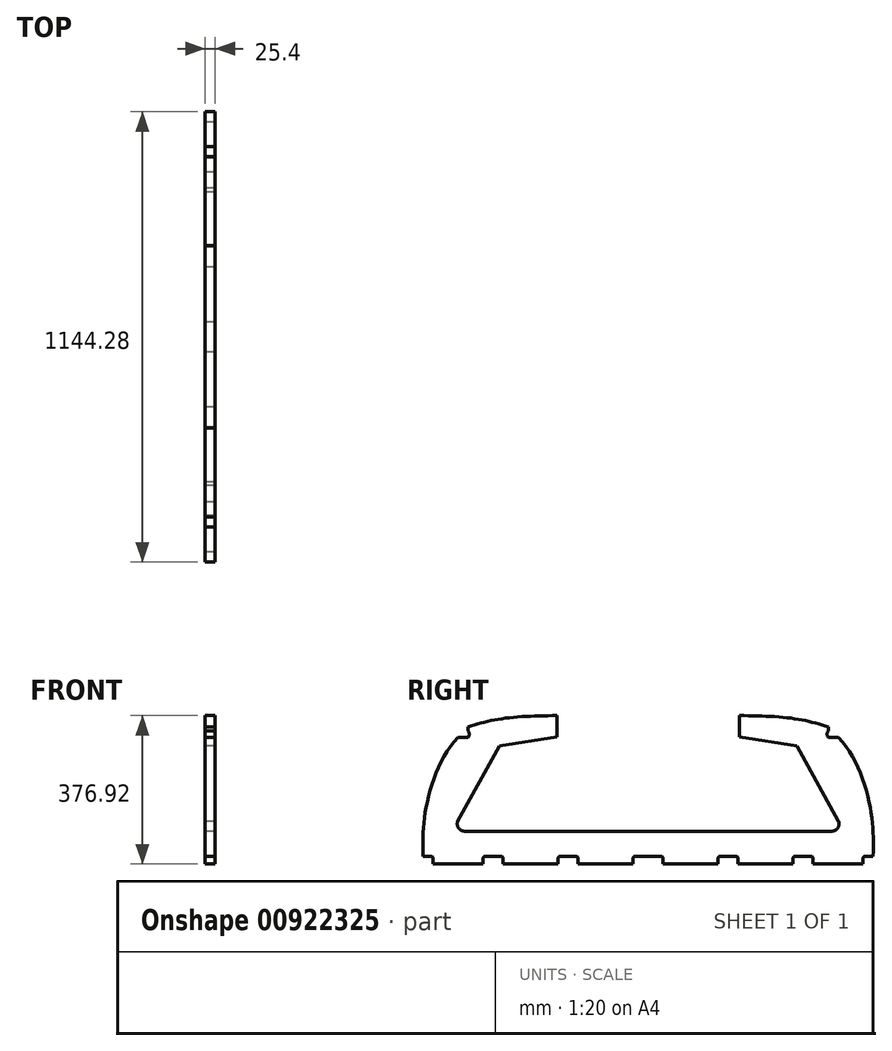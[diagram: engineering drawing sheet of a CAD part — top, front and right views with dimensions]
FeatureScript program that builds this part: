
annotation { "Feature Type Name" : "Feature", "Feature Type Description" : "" }
export const myFeature = defineFeature(function(context is Context, id is Id, definition is map)
    precondition{}
    {
        {
            var Q0;
            Q0=qCreatedBy(makeId("Right.planeOp"),FACE);
            var sketch = newSketch(context, id + "F0", { "sketchPlane" : qUnion([Q0])});
            skLineSegment(sketch, "E0", {"start": v(0, -94.79) * mm, "end": v(-33.02, -94.79) * mm});
            skLineSegment(sketch, "E1", {"start": v(-38.1, -99.87) * mm, "end": v(-38.1, -113.84) * mm});
            skLineSegment(sketch, "E2", {"start": v(-38.1, -113.84) * mm, "end": v(-177.8, -113.84) * mm});
            skLineSegment(sketch, "E3", {"start": v(-177.8, -113.84) * mm, "end": v(-177.8, -99.87) * mm});
            skLineSegment(sketch, "E4", {"start": v(-182.88, -94.79) * mm, "end": v(-223.52, -94.79) * mm});
            skLineSegment(sketch, "E5", {"start": v(-228.6, -99.87) * mm, "end": v(-228.6, -113.84) * mm});
            skLineSegment(sketch, "E6", {"start": v(-228.6, -113.84) * mm, "end": v(-368.3, -113.84) * mm});
            skLineSegment(sketch, "E7", {"start": v(-368.3, -113.84) * mm, "end": v(-368.3, -99.87) * mm});
            skLineSegment(sketch, "E8", {"start": v(-373.38, -94.79) * mm, "end": v(-414.02, -94.79) * mm});
            skLineSegment(sketch, "E9", {"start": v(-419.1, -99.87) * mm, "end": v(-419.1, -113.84) * mm});
            skLineSegment(sketch, "E10", {"start": v(-419.1, -113.84) * mm, "end": v(-546.1, -113.84) * mm});
            skLineSegment(sketch, "E11", {"start": v(-546.1, -113.84) * mm, "end": v(-546.1, -99.87) * mm});
            skLineSegment(sketch, "E12", {"start": v(-551.18, -94.79) * mm, "end": v(-571.5, -94.79) * mm});
            skLineSegment(sketch, "E13", {"start": v(-465.99, -30.95) * mm, "end": v(0, -30.95) * mm});
            skPoint(sketch, "E14.visualSharp", {"position": v(-419.1, -94.79) * mm});
            skArc(sketch, "E14.filletArc", {"start": v(-414.02, -94.79) * mm, "mid": v(-417.61, -96.28) * mm, "end": v(-419.1, -99.87) * mm});
            skPoint(sketch, "E15.visualSharp", {"position": v(-368.3, -94.79) * mm});
            skArc(sketch, "E15.filletArc", {"start": v(-368.3, -99.87) * mm, "mid": v(-369.79, -96.28) * mm, "end": v(-373.38, -94.79) * mm});
            skPoint(sketch, "E16.visualSharp", {"position": v(-228.6, -94.79) * mm});
            skArc(sketch, "E16.filletArc", {"start": v(-223.52, -94.79) * mm, "mid": v(-227.11, -96.28) * mm, "end": v(-228.6, -99.87) * mm});
            skPoint(sketch, "E17.visualSharp", {"position": v(-177.8, -94.79) * mm});
            skArc(sketch, "E17.filletArc", {"start": v(-177.8, -99.87) * mm, "mid": v(-179.29, -96.28) * mm, "end": v(-182.88, -94.79) * mm});
            skPoint(sketch, "E18.visualSharp", {"position": v(-38.1, -94.79) * mm});
            skArc(sketch, "E18.filletArc", {"start": v(-33.02, -94.79) * mm, "mid": v(-36.61, -96.28) * mm, "end": v(-38.1, -99.87) * mm});
            skPoint(sketch, "E19.visualSharp", {"position": v(-546.1, -94.79) * mm});
            skArc(sketch, "E19.filletArc", {"start": v(-546.1, -99.87) * mm, "mid": v(-547.59, -96.28) * mm, "end": v(-551.18, -94.79) * mm});
            skPoint(sketch, "E20.visualSharp", {"position": v(-423.74, 200.49) * mm});
            skPoint(sketch, "E21.visualSharp", {"position": v(-493.39, -30.95) * mm});
            skArc(sketch, "E21.filletArc", {"start": v(-483.93, -5.23) * mm, "mid": v(-481.66, -22.77) * mm, "end": v(-465.99, -30.95) * mm});
            skArc(sketch, "E22", {"start": v(-457.61, 207.28) * mm, "mid": v(-454.45, 215.67) * mm, "end": v(-457.61, 224.06) * mm});
            skFitSpline(sketch, "E23", {"points": [v(-460.76, 233.62) * mm, v(-370.5, 255.33) * mm, v(-232.08, 263.08) * mm], "startDerivative": vector(189.06, 55.92) * mm, "endDerivative": vector(265.74, 4.72) * mm});
            skLineSegment(sketch, "E24", {"start": v(-457.61, 207.28) * mm, "end": v(-483.01, 207.28) * mm});
            skLineSegment(sketch, "E25", {"start": v(-457.61, 224.06) * mm, "end": v(-457.61, 234.55) * mm});
            skLineSegment(sketch, "E26", {"start": v(-483.93, -5.23) * mm, "end": v(-377.52, 186.4) * mm});
            skLineSegment(sketch, "E27", {"start": v(-232.08, 263.08) * mm, "end": v(-232.08, 209.2) * mm});
            skLineSegment(sketch, "E28", {"start": v(-377.52, 186.4) * mm, "end": v(-232.08, 209.2) * mm});
            skFitSpline(sketch, "E29", {"points": [v(-571.5, -94.79) * mm, v(-562.79, 36.53) * mm, v(-483.01, 207.28) * mm], "startDerivative": vector(-9.83, 282.77) * mm, "endDerivative": vector(236.5, 235.39) * mm});
            skArc(sketch, "E30.MirrorCS", {"start": v(177.8, -99.87) * mm, "mid": v(179.29, -96.28) * mm, "end": v(182.88, -94.79) * mm});
            skArc(sketch, "E31.MirrorCS", {"start": v(414.02, -94.79) * mm, "mid": v(417.61, -96.28) * mm, "end": v(419.1, -99.87) * mm});
            skLineSegment(sketch, "E32.MirrorCS", {"start": v(457.61, 224.06) * mm, "end": v(457.61, 234.55) * mm});
            skArc(sketch, "E33.MirrorCS", {"start": v(33.02, -94.79) * mm, "mid": v(36.61, -96.28) * mm, "end": v(38.1, -99.87) * mm});
            skArc(sketch, "E34.MirrorCS", {"start": v(223.52, -94.79) * mm, "mid": v(227.11, -96.28) * mm, "end": v(228.6, -99.87) * mm});
            skArc(sketch, "E35.MirrorCS", {"start": v(368.3, -99.87) * mm, "mid": v(369.79, -96.28) * mm, "end": v(373.38, -94.79) * mm});
            skArc(sketch, "E36.MirrorCS", {"start": v(546.1, -99.87) * mm, "mid": v(547.59, -96.28) * mm, "end": v(551.18, -94.79) * mm});
            skLineSegment(sketch, "E37.MirrorCS", {"start": v(551.18, -94.79) * mm, "end": v(571.5, -94.79) * mm});
            skLineSegment(sketch, "E38.MirrorCS", {"start": v(228.6, -99.87) * mm, "end": v(228.6, -113.84) * mm});
            skLineSegment(sketch, "E39.MirrorCS", {"start": v(368.3, -113.84) * mm, "end": v(368.3, -99.87) * mm});
            skLineSegment(sketch, "E40.MirrorCS", {"start": v(38.1, -99.87) * mm, "end": v(38.1, -113.84) * mm});
            skLineSegment(sketch, "E41.MirrorCS", {"start": v(457.61, 207.28) * mm, "end": v(483.01, 207.28) * mm});
            skLineSegment(sketch, "E42.MirrorCS", {"start": v(546.1, -113.84) * mm, "end": v(546.1, -99.87) * mm});
            skLineSegment(sketch, "E43.MirrorCS", {"start": v(419.1, -99.87) * mm, "end": v(419.1, -113.84) * mm});
            skLineSegment(sketch, "E44.MirrorCS", {"start": v(177.8, -113.84) * mm, "end": v(177.8, -99.87) * mm});
            skArc(sketch, "E45.MirrorCS", {"start": v(457.61, 207.28) * mm, "mid": v(454.45, 215.67) * mm, "end": v(457.61, 224.06) * mm});
            skLineSegment(sketch, "E46.MirrorCS", {"start": v(373.38, -94.79) * mm, "end": v(414.02, -94.79) * mm});
            skPoint(sketch, "E47.MirrorP", {"position": v(419.1, -94.79) * mm});
            skLineSegment(sketch, "E48.MirrorCS", {"start": v(465.99, -30.95) * mm, "end": v(0, -30.95) * mm});
            skLineSegment(sketch, "E49.MirrorCS", {"start": v(0, -94.79) * mm, "end": v(33.02, -94.79) * mm});
            skPoint(sketch, "E50.MirrorP", {"position": v(228.6, -94.79) * mm});
            skLineSegment(sketch, "E51.MirrorCS", {"start": v(483.93, -5.23) * mm, "end": v(377.52, 186.4) * mm});
            skLineSegment(sketch, "E52.MirrorCS", {"start": v(38.1, -113.84) * mm, "end": v(177.8, -113.84) * mm});
            skPoint(sketch, "E53.MirrorP", {"position": v(493.39, -30.95) * mm});
            skArc(sketch, "E54.MirrorCS", {"start": v(483.93, -5.23) * mm, "mid": v(481.66, -22.77) * mm, "end": v(465.99, -30.95) * mm});
            skLineSegment(sketch, "E55.MirrorCS", {"start": v(377.52, 186.4) * mm, "end": v(232.08, 209.2) * mm});
            skLineSegment(sketch, "E56.MirrorCS", {"start": v(232.08, 263.08) * mm, "end": v(232.08, 209.2) * mm});
            skLineSegment(sketch, "E57.MirrorCS", {"start": v(419.1, -113.84) * mm, "end": v(546.1, -113.84) * mm});
            skLineSegment(sketch, "E58.MirrorCS", {"start": v(182.88, -94.79) * mm, "end": v(223.52, -94.79) * mm});
            skLineSegment(sketch, "E59.MirrorCS", {"start": v(228.6, -113.84) * mm, "end": v(368.3, -113.84) * mm});
            skPoint(sketch, "E60.MirrorP", {"position": v(177.8, -94.79) * mm});
            skPoint(sketch, "E61.MirrorP", {"position": v(368.3, -94.79) * mm});
            skPoint(sketch, "E62.MirrorP", {"position": v(423.74, 200.49) * mm});
            skPoint(sketch, "E63.MirrorP", {"position": v(546.1, -94.79) * mm});
            skFitSpline(sketch, "E64.MirrorCS", {"points": [v(571.5, -94.79) * mm, v(562.79, 36.53) * mm, v(483.01, 207.28) * mm], "startDerivative": vector(9.83, 282.77) * mm, "endDerivative": vector(-236.5, 235.39) * mm});
            skFitSpline(sketch, "E65.MirrorCS", {"points": [v(460.76, 233.62) * mm, v(370.5, 255.33) * mm, v(232.08, 263.08) * mm], "startDerivative": vector(-189.06, 55.92) * mm, "endDerivative": vector(-265.74, 4.72) * mm});
            skPoint(sketch, "E66.MirrorP", {"position": v(38.1, -94.79) * mm});
            skSolve(sketch);
        }
        {
            var Q0;
            Q0=makeQuery(id+"F0.imprint","IMPRINT",FACE,{"disambiguationData":[TD([[makeQuery(id+"F0.imprint","IMPRINT",EDGE,{"derivedFrom":sQuery(id+"F0.wireOp",EDGE,"E0")}),-1.0]])]});
            extrude(context, id + "F1", {"entities" : qUnion([Q0]), "depth" : 25.4 * mm, "offsetDistance" : 25.4 * mm});
        }
    });
